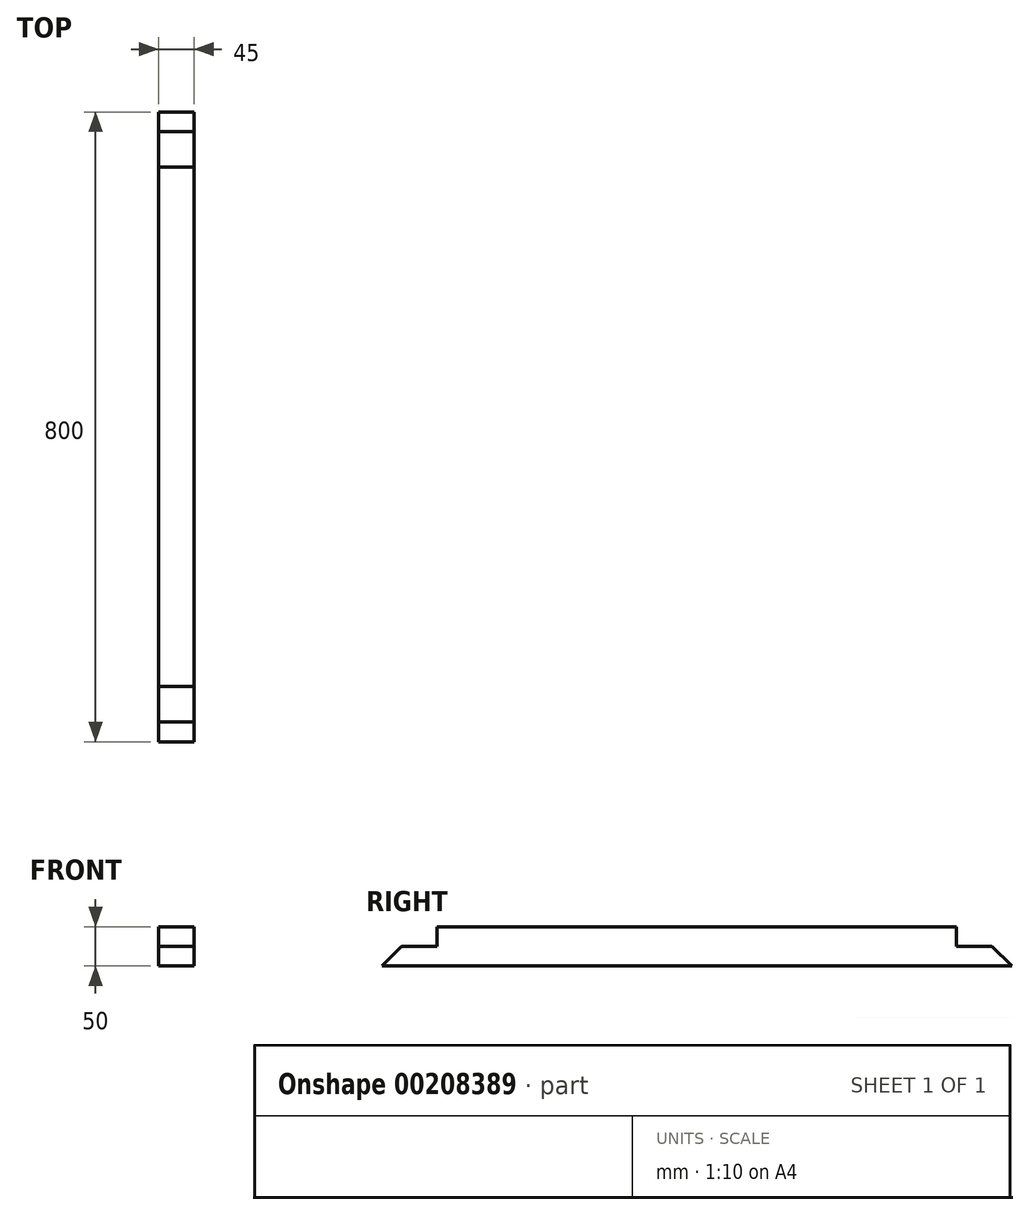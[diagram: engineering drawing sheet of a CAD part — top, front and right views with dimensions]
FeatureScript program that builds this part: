
annotation { "Feature Type Name" : "Feature", "Feature Type Description" : "" }
export const myFeature = defineFeature(function(context is Context, id is Id, definition is map)
    precondition{}
    {
        {
            var Q0;
            Q0=qCreatedBy(makeId("Front.planeOp"),FACE);
            var sketch = newSketch(context, id + "F0", { "sketchPlane" : qUnion([Q0])});
            skLineSegment(sketch, "E0.bottom", {"start": v(-22.5, 12.5) * mm, "end": v(22.5, 12.5) * mm});
            skLineSegment(sketch, "E0.top", {"start": v(-22.5, -12.5) * mm, "end": v(22.5, -12.5) * mm});
            skLineSegment(sketch, "E0.left", {"start": v(-22.5, 12.5) * mm, "end": v(-22.5, -12.5) * mm});
            skLineSegment(sketch, "E0.right", {"start": v(22.5, 12.5) * mm, "end": v(22.5, -12.5) * mm});
            skSolve(sketch);
        }
        {
            var Q0;
            Q0=makeQuery(id+"F0.imprint","IMPRINT",FACE,{"disambiguationData":[TD([[makeQuery(id+"F0.imprint","IMPRINT",EDGE,{"derivedFrom":sQuery(id+"F0.wireOp",EDGE,"E0.bottom")}),-1.0]])]});
            extrude(context, id + "F1", {"entities" : qUnion([Q0]), "oppositeDirection" : true, "depth" : 800 * mm});
        }
        {
            var Q0;
            Q0=makeQuery(id+"F1.opExtrude","SWEPT_FACE",FACE,{"disambiguationData":[OSD([sQuery(id+"F0.wireOp",EDGE,"E0.right")])]});
            var sketch = newSketch(context, id + "F2", { "sketchPlane" : qUnion([Q0])});
            skLineSegment(sketch, "E1", {"start": v(0, -12.5) * mm, "end": v(25, 12.5) * mm});
            skLineSegment(sketch, "E2", {"start": v(25, 12.5) * mm, "end": v(0, 12.5) * mm});
            skLineSegment(sketch, "E3", {"start": v(0, 12.5) * mm, "end": v(0, -12.5) * mm});
            skSolve(sketch);
        }
        {
            var Q0;
            Q0=makeQuery(id+"F2.imprint","IMPRINT",FACE,{"disambiguationData":[TD([[makeQuery(id+"F2.imprint","IMPRINT",EDGE,{"derivedFrom":sQuery(id+"F2.wireOp",EDGE,"E1")}),1.0]])]});
            extrude(context, id + "F3", {"entities" : qUnion([Q0]), "operationType" : NewBodyOperationType.REMOVE, "oppositeDirection" : true, "depth" : 45 * mm});
        }
        {
            var Q0;
            Q0=makeQuery(id+"F1.opExtrude","SWEPT_FACE",FACE,{"disambiguationData":[OSD([sQuery(id+"F0.wireOp",EDGE,"E0.left")])]});
            var sketch = newSketch(context, id + "F4", { "sketchPlane" : qUnion([Q0])});
            skLineSegment(sketch, "E4", {"start": v(-800, -12.5) * mm, "end": v(-775, 12.5) * mm});
            skLineSegment(sketch, "E5", {"start": v(-775, 12.5) * mm, "end": v(-800, 12.5) * mm});
            skLineSegment(sketch, "E6", {"start": v(-800, 12.5) * mm, "end": v(-800, -12.5) * mm});
            skSolve(sketch);
        }
        {
            var Q0;
            Q0=makeQuery(id+"F4.imprint","IMPRINT",FACE,{"disambiguationData":[TD([[makeQuery(id+"F4.imprint","IMPRINT",EDGE,{"derivedFrom":sQuery(id+"F4.wireOp",EDGE,"E4")}),1.0]])]});
            extrude(context, id + "F5", {"entities" : qUnion([Q0]), "operationType" : NewBodyOperationType.REMOVE, "oppositeDirection" : true, "depth" : 45 * mm});
        }
        {
            var Q0;
            Q0=qCreatedBy(makeId("Front.planeOp"),FACE);
            var sketch = newSketch(context, id + "F6", { "sketchPlane" : qUnion([Q0])});
            skLineSegment(sketch, "E7", {"start": v(-22.5, 12.5) * mm, "end": v(-22.5, 37.5) * mm});
            skLineSegment(sketch, "E8", {"start": v(-22.5, 37.5) * mm, "end": v(22.5, 37.5) * mm});
            skLineSegment(sketch, "E9", {"start": v(22.5, 37.5) * mm, "end": v(22.5, 12.5) * mm});
            skLineSegment(sketch, "E10", {"start": v(-22.5, 12.5) * mm, "end": v(22.5, 12.5) * mm});
            skSolve(sketch);
        }
        {
            var Q0;
            Q0=makeQuery(id+"F6.imprint","IMPRINT",FACE,{"disambiguationData":[TD([[makeQuery(id+"F6.imprint","IMPRINT",EDGE,{"derivedFrom":sQuery(id+"F6.wireOp",EDGE,"E7")}),-1.0]])]});
            extrude(context, id + "F7", {"entities" : qUnion([Q0]), "operationType" : NewBodyOperationType.ADD, "oppositeDirection" : true, "depth" : 800 * mm});
        }
        {
            var Q0;
            Q0=makeQuery(id+"F7.boolean.opBoolean","MERGE",FACE,{"derivedFrom":[makeQuery(id+"F1.opExtrude","SWEPT_FACE",FACE,{"disambiguationData":[OSD([sQuery(id+"F0.wireOp",EDGE,"E0.left")])]}),makeQuery(id+"F7.opExtrude","SWEPT_FACE",FACE,{"disambiguationData":[OSD([sQuery(id+"F6.wireOp",EDGE,"E7")])]})]});
            var sketch = newSketch(context, id + "F8", { "sketchPlane" : qUnion([Q0])});
            skLineSegment(sketch, "E11.bottom", {"start": v(-800, 37.5) * mm, "end": v(-730, 37.5) * mm});
            skLineSegment(sketch, "E11.top", {"start": v(-800, 12.5) * mm, "end": v(-730, 12.5) * mm});
            skLineSegment(sketch, "E11.left", {"start": v(-800, 37.5) * mm, "end": v(-800, 12.5) * mm});
            skLineSegment(sketch, "E11.right", {"start": v(-730, 37.5) * mm, "end": v(-730, 12.5) * mm});
            skSolve(sketch);
        }
        {
            var Q0;
            Q0=makeQuery(id+"F8.imprint","IMPRINT",FACE,{"disambiguationData":[TD([[makeQuery(id+"F8.imprint","IMPRINT",EDGE,{"derivedFrom":sQuery(id+"F8.wireOp",EDGE,"E11.bottom")}),-1.0]])]});
            extrude(context, id + "F9", {"entities" : qUnion([Q0]), "operationType" : NewBodyOperationType.REMOVE, "oppositeDirection" : true, "depth" : 45 * mm});
        }
        {
            var Q0;
            Q0=makeQuery(id+"F7.boolean.opBoolean","MERGE",FACE,{"derivedFrom":[makeQuery(id+"F1.opExtrude","SWEPT_FACE",FACE,{"disambiguationData":[OSD([sQuery(id+"F0.wireOp",EDGE,"E0.left")])]}),makeQuery(id+"F7.opExtrude","SWEPT_FACE",FACE,{"disambiguationData":[OSD([sQuery(id+"F6.wireOp",EDGE,"E7")])]})]});
            var sketch = newSketch(context, id + "F10", { "sketchPlane" : qUnion([Q0])});
            skPoint(sketch, "E12.oppositeSnap0", {"position": v(-12.5, 12.5) * mm});
            skLineSegment(sketch, "E12.bottom", {"start": v(0, 37.5) * mm, "end": v(-70, 37.5) * mm});
            skLineSegment(sketch, "E12.top", {"start": v(0, 12.5) * mm, "end": v(-70, 12.5) * mm});
            skLineSegment(sketch, "E12.left", {"start": v(0, 37.5) * mm, "end": v(0, 12.5) * mm});
            skLineSegment(sketch, "E12.right", {"start": v(-70, 37.5) * mm, "end": v(-70, 12.5) * mm});
            skSolve(sketch);
        }
        {
            var Q0;
            Q0=makeQuery(id+"F10.imprint","IMPRINT",FACE,{"disambiguationData":[TD([[makeQuery(id+"F10.imprint","IMPRINT",EDGE,{"derivedFrom":sQuery(id+"F10.wireOp",EDGE,"E12.bottom")}),-1.0]])]});
            extrude(context, id + "F11", {"entities" : qUnion([Q0]), "operationType" : NewBodyOperationType.REMOVE, "oppositeDirection" : true, "depth" : 45 * mm});
        }
    });
